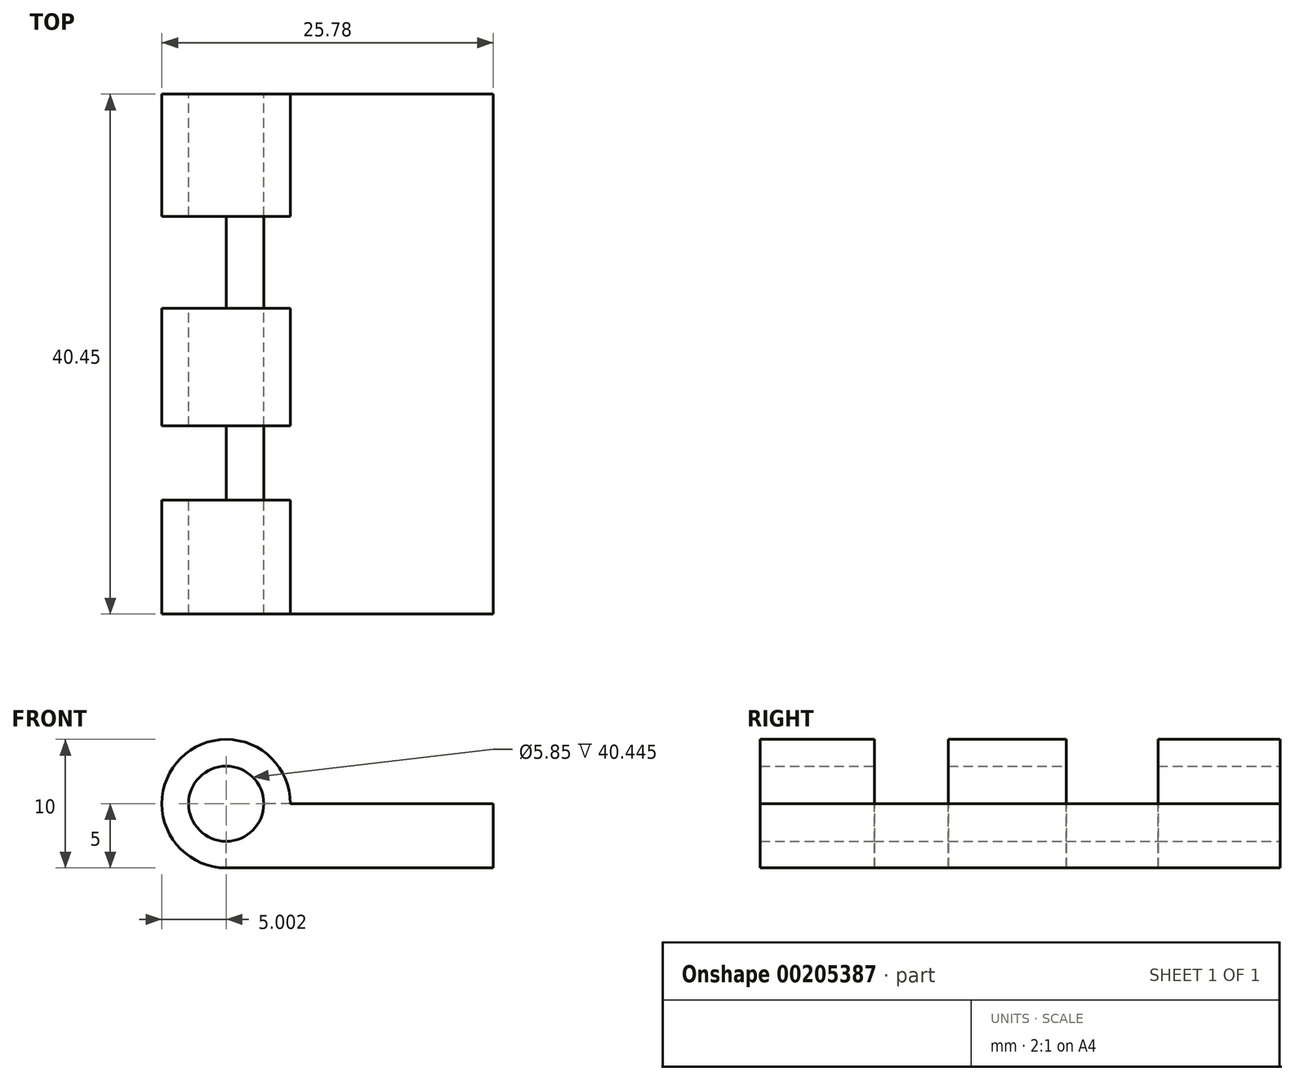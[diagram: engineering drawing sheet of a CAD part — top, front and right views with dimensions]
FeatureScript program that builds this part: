
annotation { "Feature Type Name" : "Feature", "Feature Type Description" : "" }
export const myFeature = defineFeature(function(context is Context, id is Id, definition is map)
    precondition{}
    {
        {
            var Q0;
            Q0=qCreatedBy(makeId("Top.planeOp"),FACE);
            var sketch = newSketch(context, id + "F0", { "sketchPlane" : qUnion([Q0])});
            skLineSegment(sketch, "E0.bottom", {"start": v(-74.86, 50.7) * mm, "end": v(-54.08, 50.7) * mm});
            skLineSegment(sketch, "E0.top", {"start": v(-74.86, 10.25) * mm, "end": v(-54.08, 10.25) * mm});
            skLineSegment(sketch, "E0.left", {"start": v(-74.86, 50.7) * mm, "end": v(-74.86, 10.25) * mm});
            skLineSegment(sketch, "E0.right", {"start": v(-54.08, 50.7) * mm, "end": v(-54.08, 10.25) * mm});
            skSolve(sketch);
        }
        {
            var Q0;
            Q0=makeQuery(id+"F0.imprint","IMPRINT",FACE,{"disambiguationData":[TD([[makeQuery(id+"F0.imprint","IMPRINT",EDGE,{"derivedFrom":sQuery(id+"F0.wireOp",EDGE,"E0.bottom")}),-1.0]])]});
            extrude(context, id + "F1", {"entities" : qUnion([Q0]), "depth" : 5 * mm});
        }
        {
            var Q0;
            Q0=makeQuery(id+"F1.opExtrude","SWEPT_FACE",FACE,{"disambiguationData":[OSD([sQuery(id+"F0.wireOp",EDGE,"E0.left")])]});
            var sketch = newSketch(context, id + "F2", { "sketchPlane" : qUnion([Q0])});
            skLineSegment(sketch, "E1.bottom", {"start": v(-50.7, 0) * mm, "end": v(-41.19, 0) * mm});
            skLineSegment(sketch, "E1.top", {"start": v(-50.7, 5) * mm, "end": v(-41.19, 5) * mm});
            skLineSegment(sketch, "E1.left", {"start": v(-50.7, 0) * mm, "end": v(-50.7, 5) * mm});
            skLineSegment(sketch, "E1.right", {"start": v(-41.19, 0) * mm, "end": v(-41.19, 5) * mm});
            skLineSegment(sketch, "E2.bottom", {"start": v(-10.25, 0) * mm, "end": v(-19.12, 0) * mm});
            skLineSegment(sketch, "E2.top", {"start": v(-10.25, 5) * mm, "end": v(-19.12, 5) * mm});
            skLineSegment(sketch, "E2.left", {"start": v(-10.25, 0) * mm, "end": v(-10.25, 5) * mm});
            skLineSegment(sketch, "E2.right", {"start": v(-19.12, 0) * mm, "end": v(-19.12, 5) * mm});
            skLineSegment(sketch, "E3.bottom", {"start": v(-24.89, 0) * mm, "end": v(-34.05, 0) * mm});
            skLineSegment(sketch, "E3.top", {"start": v(-24.89, 5) * mm, "end": v(-34.05, 5) * mm});
            skLineSegment(sketch, "E3.left", {"start": v(-24.89, 0) * mm, "end": v(-24.89, 5) * mm});
            skLineSegment(sketch, "E3.right", {"start": v(-34.05, 0) * mm, "end": v(-34.05, 5) * mm});
            skLineSegment(sketch, "E4", {"start": v(-52.77, 5) * mm, "end": v(-5.1, 5) * mm, "construction": true});
            skSolve(sketch);
        }
        {
            var Q0;
            Q0=makeQuery(id+"F2.imprint","IMPRINT",FACE,{"disambiguationData":[TD([[makeQuery(id+"F2.imprint","IMPRINT",EDGE,{"derivedFrom":sQuery(id+"F2.wireOp",EDGE,"E1.bottom")}),1.0]])]});
            var Q1;
            Q1=makeQuery(id+"F2.imprint","IMPRINT",FACE,{"disambiguationData":[TD([[makeQuery(id+"F2.imprint","IMPRINT",EDGE,{"derivedFrom":sQuery(id+"F2.wireOp",EDGE,"E3.bottom")}),1.0]])]});
            var Q2;
            Q2=makeQuery(id+"F2.imprint","IMPRINT",FACE,{"disambiguationData":[TD([[makeQuery(id+"F2.imprint","IMPRINT",EDGE,{"derivedFrom":sQuery(id+"F2.wireOp",EDGE,"E2.bottom")}),1.0]])]});
            var Q3;
            Q3=sQuery(id+"F2.wireOp",EDGE,"E4");
            revolve(context, id + "F3", {"operationType" : NewBodyOperationType.ADD, "entities" : qUnion([Q0, Q1, Q2]), "axis" : qUnion([Q3]), "revolveType" : RevolveType.ONE_DIRECTION, "oppositeDirection" : true, "angle" : 270 * degree});
        }
        {
            var Q0;
            Q0=makeQuery(id+"F3.boolean.opBoolean","MERGE",FACE,{"derivedFrom":[makeQuery(id+"F1.opExtrude","SWEPT_FACE",FACE,{"disambiguationData":[OSD([sQuery(id+"F0.wireOp",EDGE,"E0.bottom")])]}),makeQuery(id+"F3.opRevolve","SWEPT_FACE",FACE,{"disambiguationData":[OSD([sQuery(id+"F2.wireOp",EDGE,"E1.left")])]})]});
            var sketch = newSketch(context, id + "F4", { "sketchPlane" : qUnion([Q0])});
            skCircle(sketch, "E5", {"center": v(74.86, 5) * mm, "radius": 2.92 * mm});
            skSolve(sketch);
        }
        {
            var Q0;
            Q0=makeQuery(id+"F4.imprint","IMPRINT",FACE,{"disambiguationData":[TD([[makeQuery(id+"F4.imprint","IMPRINT",EDGE,{"derivedFrom":sQuery(id+"F4.wireOp",EDGE,"E5")}),1.0]])]});
            extrude(context, id + "F5", {"entities" : qUnion([Q0]), "operationType" : NewBodyOperationType.REMOVE, "oppositeDirection" : true, "depth" : 100 * mm});
        }
    });
